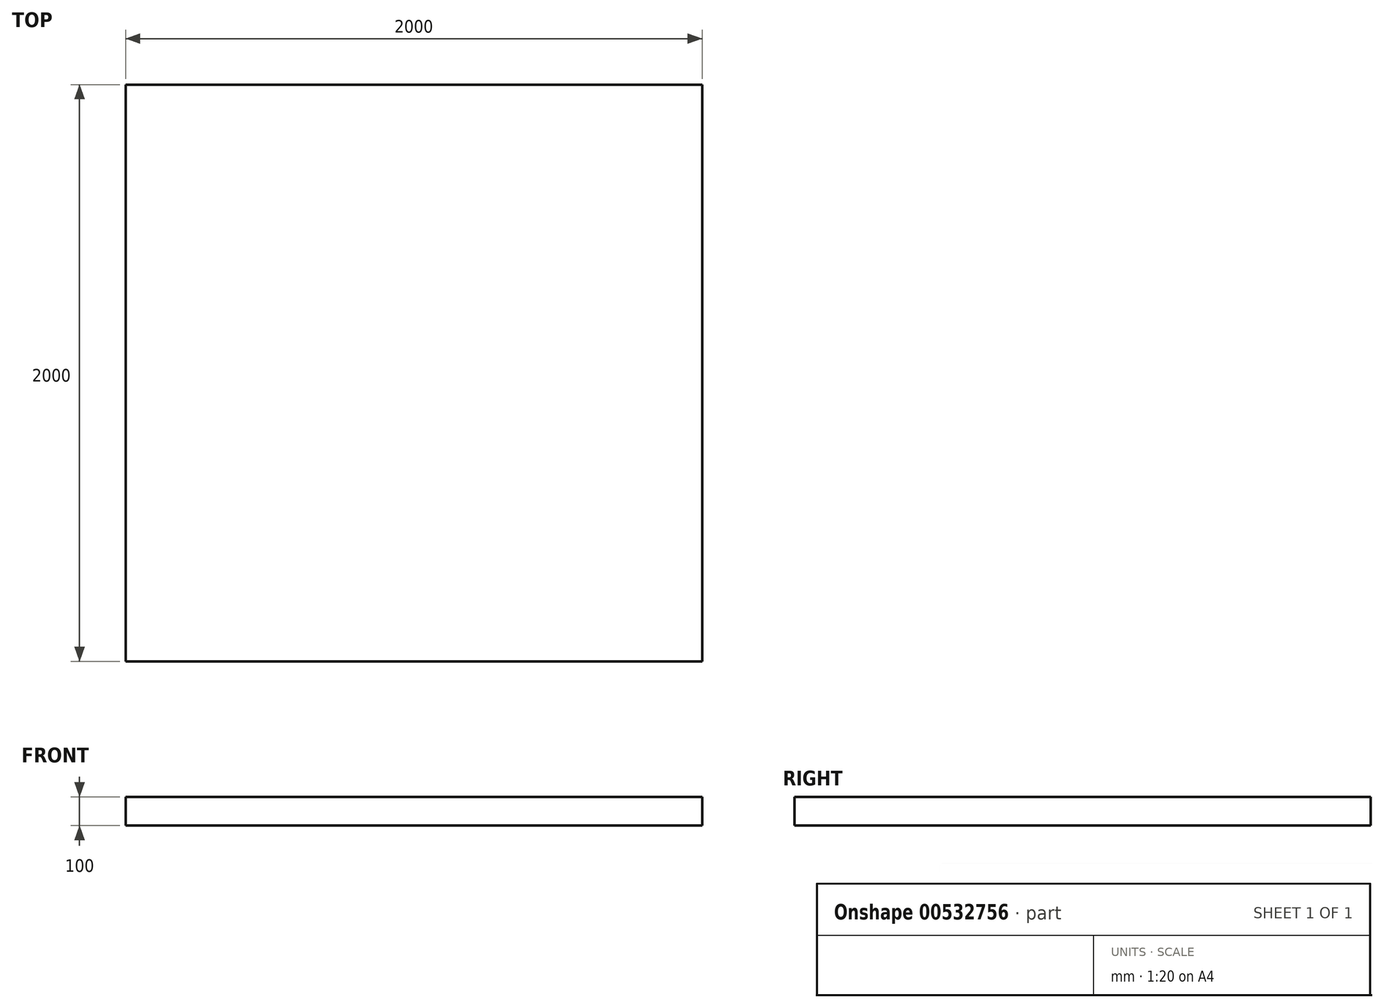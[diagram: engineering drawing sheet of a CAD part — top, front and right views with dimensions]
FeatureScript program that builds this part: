
annotation { "Feature Type Name" : "Feature", "Feature Type Description" : "" }
export const myFeature = defineFeature(function(context is Context, id is Id, definition is map)
    precondition{}
    {
        {
            var Q0;
            Q0=qCreatedBy(makeId("Top.planeOp"),FACE);
            var sketch = newSketch(context, id + "F0", { "sketchPlane" : qUnion([Q0])});
            skLineSegment(sketch, "E0.bottom", {"start": v(0, 0) * mm, "end": v(2000, 0) * mm});
            skLineSegment(sketch, "E0.top", {"start": v(0, 2000) * mm, "end": v(2000, 2000) * mm});
            skLineSegment(sketch, "E0.left", {"start": v(0, 0) * mm, "end": v(0, 2000) * mm});
            skLineSegment(sketch, "E0.right", {"start": v(2000, 0) * mm, "end": v(2000, 2000) * mm});
            skSolve(sketch);
        }
        {
            var Q0;
            Q0=makeQuery(id+"F0.imprint","IMPRINT",FACE,{"disambiguationData":[TD([[makeQuery(id+"F0.imprint","IMPRINT",EDGE,{"derivedFrom":sQuery(id+"F0.wireOp",EDGE,"E0.bottom")}),1.0]])]});
            extrude(context, id + "F1", {"entities" : qUnion([Q0]), "depth" : 100 * mm, "offsetDistance" : 25 * mm});
        }
    });
